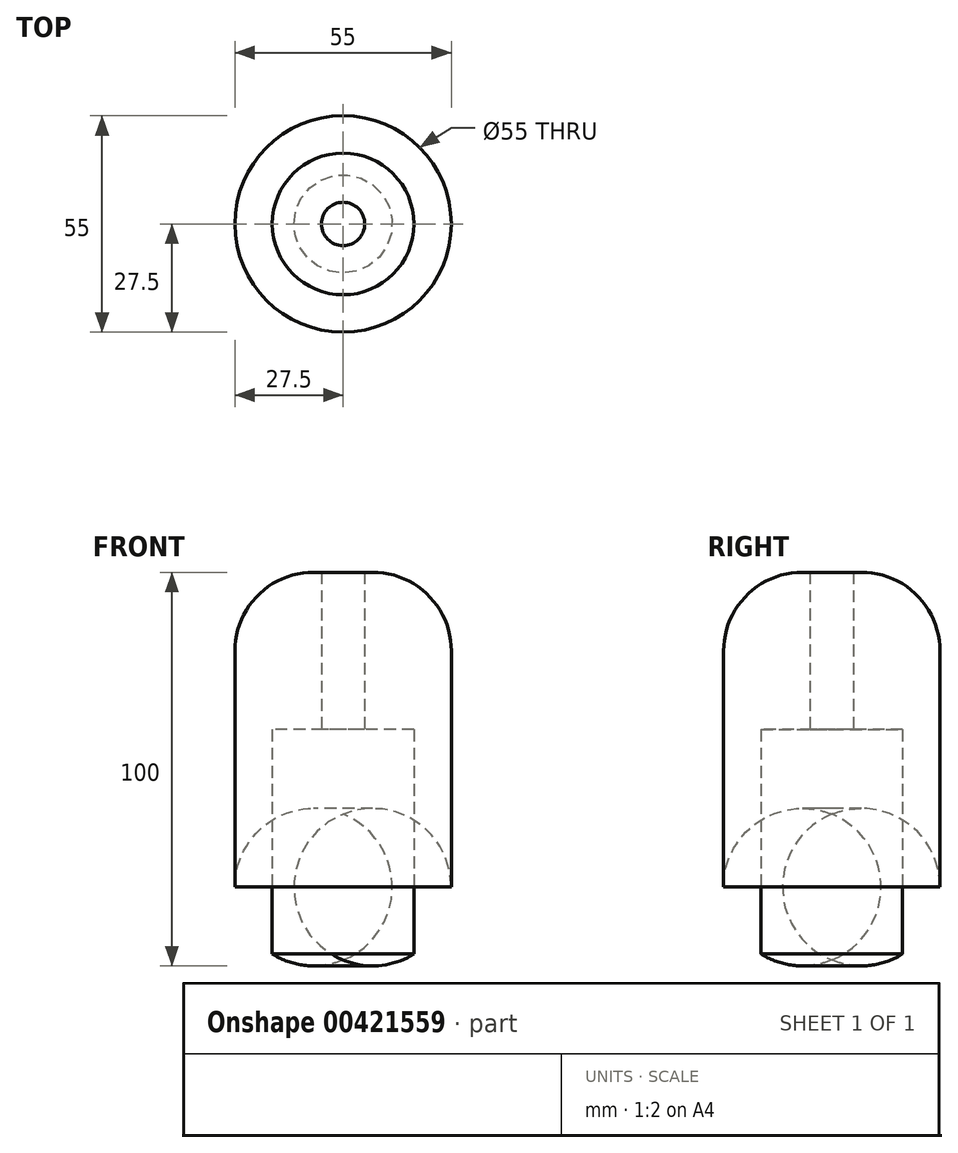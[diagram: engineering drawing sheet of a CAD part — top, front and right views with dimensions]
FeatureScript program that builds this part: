
annotation { "Feature Type Name" : "Feature", "Feature Type Description" : "" }
export const myFeature = defineFeature(function(context is Context, id is Id, definition is map)
    precondition{}
    {
        {
            var Q0;
            Q0=qCreatedBy(makeId("Top.planeOp"),FACE);
            var sketch = newSketch(context, id + "F0", { "sketchPlane" : qUnion([Q0])});
            skCircle(sketch, "E0", {"center": v(0, 0) * mm, "radius": 27.5 * mm});
            skCircle(sketch, "E1", {"center": v(0, 0) * mm, "radius": 19 * mm});
            skCircle(sketch, "E2", {"center": v(0, 0) * mm, "radius": 5.5 * mm});
            skSolve(sketch);
        }
        {
            var Q0;
            Q0=makeQuery(id+"F0.imprint","IMPRINT",FACE,{"disambiguationData":[TD([[makeQuery(id+"F0.imprint","IMPRINT",EDGE,{"derivedFrom":sQuery(id+"F0.wireOp",EDGE,"E0")}),1.0]])]});
            var Q1;
            Q1=makeQuery(id+"F0.imprint","IMPRINT",FACE,{"disambiguationData":[TD([[makeQuery(id+"F0.imprint","IMPRINT",EDGE,{"derivedFrom":sQuery(id+"F0.wireOp",EDGE,"E1")}),1.0]])]});
            var Q2;
            Q2=sQuery(id+"F0.wireOp",EDGE,"E0");
            extrude(context, id + "F1", {"entities" : qUnion([Q0, Q1]), "surfaceEntities" : qUnion([Q2]), "depth" : 100 * mm});
        }
        {
            var Q0;
            Q0=makeQuery(id+"F1.opExtrude","CAP_EDGE",EDGE,{"disambiguationData":[OSD([sQuery(id+"F0.wireOp",EDGE,"E0")])],"isStart":false});
            var Q1;
            Q1=makeQuery(id+"F1.opExtrude","CAP_EDGE",EDGE,{"disambiguationData":[OSD([sQuery(id+"F0.wireOp",EDGE,"E0")])],"isStart":true});
            fillet(context, id + "F2", {"entities" : qUnion([Q0, Q1]), "radius" : 20 * mm, "tangentPropagation" : true, "allowEdgeOverflow" : false});
        }
        {
            var Q0;
            Q0=qCreatedBy(makeId("Top.planeOp"),FACE);
            var sketch = newSketch(context, id + "F3", { "sketchPlane" : qUnion([Q0])});
            skCircle(sketch, "E3", {"center": v(0, 0) * mm, "radius": 18 * mm});
            skSolve(sketch);
        }
        {
            var Q0;
            Q0 = qSketchRegion(id + "F3", true);
            extrude(context, id + "F4", {"entities" : qUnion([Q0]), "depth" : 60 * mm});
        }
        {
            var Q0;
            Q0=makeQuery(id+"F4.opExtrude","SWEPT_BODY",BODY,{"disambiguationData":[OSD([sQuery(id+"F3.wireOp",EDGE,"E3")])]});
            var Q1;
            Q1=makeQuery(id+"F1.opExtrude","SWEPT_BODY",BODY,{"disambiguationData":[OSD([sQuery(id+"F0.wireOp",EDGE,"E0"),sQuery(id+"F0.wireOp",EDGE,"E2")])]});
            booleanBodies(context, id + "F5", {"operationType" : BooleanOperationType.SUBTRACTION, "tools" : qUnion([Q0]), "targets" : qUnion([Q1])});
        }
    });
